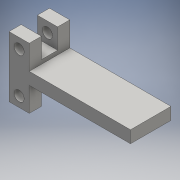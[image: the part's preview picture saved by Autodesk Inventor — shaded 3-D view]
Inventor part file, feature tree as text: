
AUTODESK INVENTOR PART (.ipt)
format: ipt  version: 2016 (Build 200138000, 138)  size: 147,456 bytes
history: native  units: mm
features: extrude x7, sketch x7, other x1
ambient origin geometry x8: Origin, YZ Plane, XZ Plane, XY Plane, X Axis, Y Axis, Z Axis, Center Point
bodies: Body1 (feature_tree)
feature tree (15):
  other  "ソリッド1"
  extrude  "押し出し1"  Depth=30.0mm
  extrude  "押し出し2"  Depth=15.0mm
  extrude  "押し出し3"  Depth=10.0mm TaperAngle=0.0deg
  extrude  "押し出し4"  Depth=25.0mm
  extrude  "押し出し5"  Depth=6.0mm
  extrude  "押し出し6"  Depth=5.0mm
  extrude  "押し出し7"  Depth=10.0mm TaperAngle=0.0deg
  sketch  "スケッチ1"
  sketch  "スケッチ2"
  sketch  "スケッチ3"
  sketch  "スケッチ4"
  sketch  "スケッチ6"
  sketch  "スケッチ7"
  sketch  "スケッチ8"
